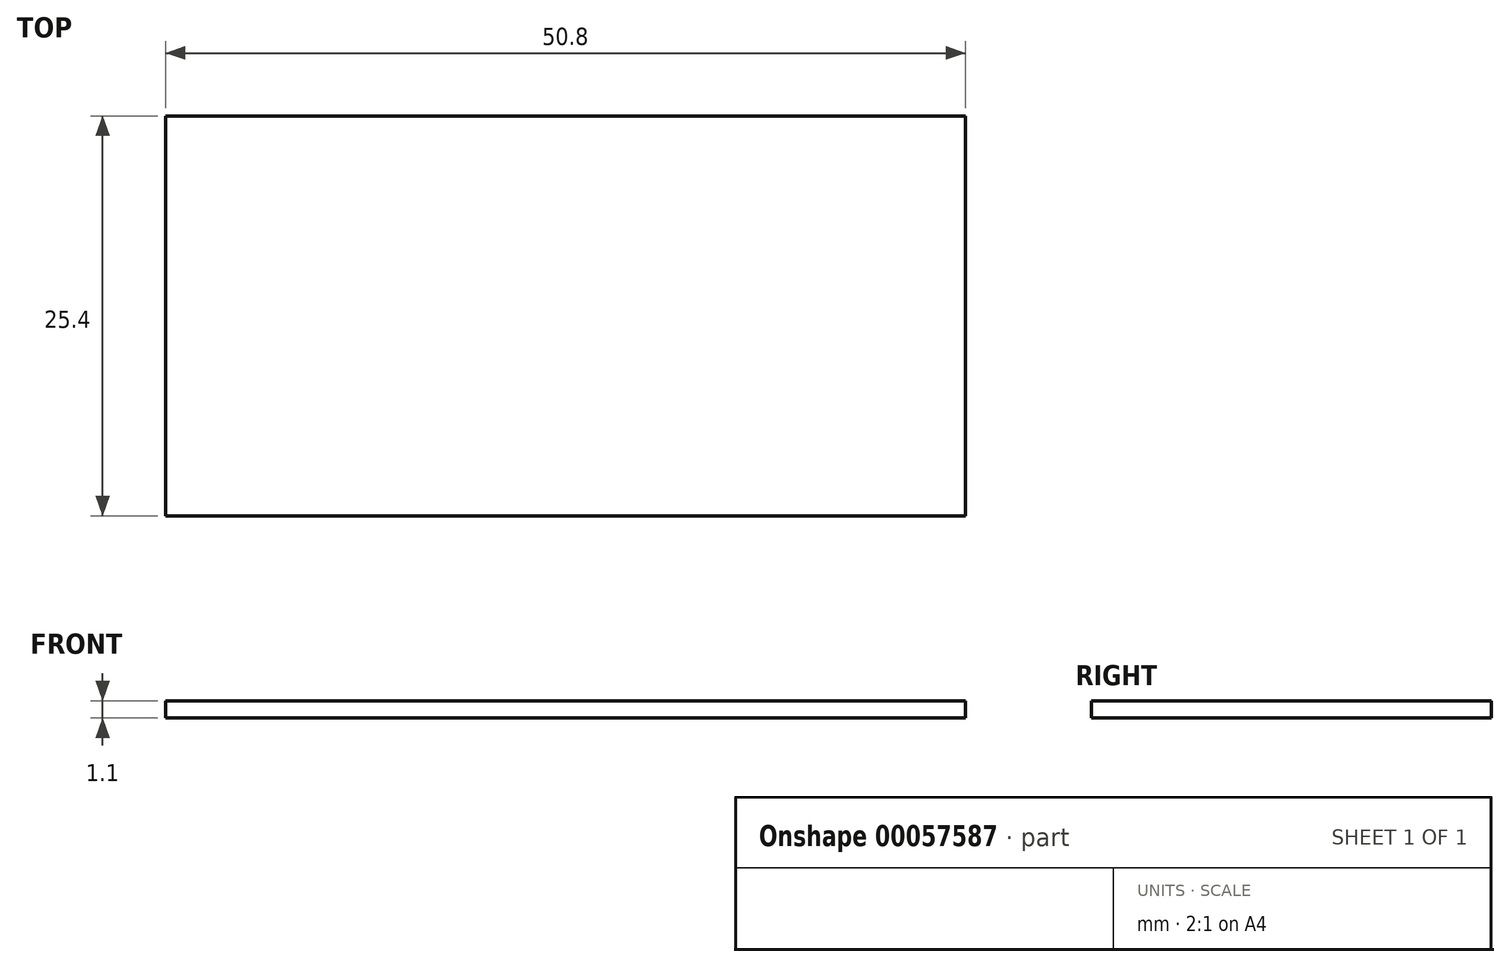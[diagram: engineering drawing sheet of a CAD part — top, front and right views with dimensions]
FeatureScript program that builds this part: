
annotation { "Feature Type Name" : "Feature", "Feature Type Description" : "" }
export const myFeature = defineFeature(function(context is Context, id is Id, definition is map)
    precondition{}
    {
        {
            var Q0;
            Q0=qCreatedBy(makeId("Top.planeOp"),FACE);
            var sketch = newSketch(context, id + "F0", { "sketchPlane" : qUnion([Q0])});
            skLineSegment(sketch, "E0.rect.bottom", {"start": v(-25.4, 12.7) * mm, "end": v(25.4, 12.7) * mm});
            skLineSegment(sketch, "E0.rect.top", {"start": v(-25.4, -12.7) * mm, "end": v(25.4, -12.7) * mm});
            skLineSegment(sketch, "E0.rect.left", {"start": v(-25.4, 12.7) * mm, "end": v(-25.4, -12.7) * mm});
            skLineSegment(sketch, "E0.rect.right", {"start": v(25.4, 12.7) * mm, "end": v(25.4, -12.7) * mm});
            skPoint(sketch, "E0.rect.middle", {"position": v(0, 0) * mm});
            skSolve(sketch);
        }
        {
            var Q0;
            Q0=makeQuery(id+"F0.imprint","IMPRINT",FACE,{"disambiguationData":[TD([[makeQuery(id+"F0.imprint","IMPRINT",EDGE,{"derivedFrom":sQuery(id+"F0.wireOp",EDGE,"E0.rect.bottom")}),-1.0]])]});
            extrude(context, id + "F1", {"entities" : qUnion([Q0]), "depth" : 1.1 * mm});
        }
    });
